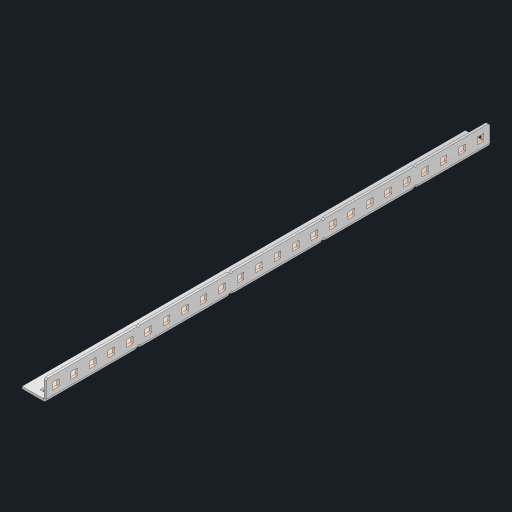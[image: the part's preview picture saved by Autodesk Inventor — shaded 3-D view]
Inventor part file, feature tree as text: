
AUTODESK INVENTOR PART (.ipt)
format: ipt  version: 2023 (Build 270158000, 158)  size: 847,360 bytes
history: native  units: in
note: dims shown in document units (in); Inventor stores cm internally (conversion verified against a paired STEP export)
features: other x53, extrude x47, sheet_metal_op x10, sketch x8, mirror x1, pattern_linear x1, chamfer x1
ambient origin geometry x8: Origin, YZ Plane, XZ Plane, XY Plane, X Axis, Y Axis, Z Axis, Center Point
bodies: Solid1 (feature_tree), Body (feature_tree)
feature tree (121):
  other  "Flange Pattern Plane"
  sheet_metal_op  "Flange Pattern"
  sheet_metal_op  "Body Pattern"
  other  "Arc Length"
  mirror  "Notch Mirror"
  pattern_linear  "Notch Pattern"  Spacing1=0.25in  [1 undecoded]
  chamfer  "End Chamfer"
  extrude  "Half Cut"  Depth=0.0625in
  sketch  "Sketch1"  dims[d0=1.5in]
  other  "Plate1"
  sketch  "Sketch2"  dims[d1=12.0in]
  other  "Plate2"
  sheet_metal_op  "Bend1"
  sheet_metal_op  "Corner1"
  sketch  "Sketch3"  dims[d2=0.0625in]
  other  "Flange Pattern Sketch"
  sketch  "Sketch7"  dims[d3=0.0625in]
  other  "Srf1"
  other  "Srf2"
  sketch  "Sketch8"  dims[d4=0.0312in]
  sketch  "Sketch9"  dims[d5=0.125in]
  other  "Srf91"
  sheet_metal_op  "Body Pattern Sketch"
  other  "Srf92"
  sketch  "Sketch13"  dims[d6=0.0625in]
  sketch  "Sketch14"  dims[d7=0.5in d8=90.0deg d9=0.0312in d10=0.25in d11=0.0625in d12=0.0625in d16=0.182in d17=0.02in d18=0.0625in d19=0.0in d20=0.25in d21=0.25in d46=0.172in d47=1.0in d48=0.0in d49=0.182in d50=0.02in d51=0.25in d52=0.25in d53=0.0625in d54=0.0in d55=0.172in d56=1.0in d57=0.0in d60=9.4488in d62=0.5in d63=0.3937in d65=0.5in d85=0.1473in d86=0.1782in d88=0.04in d89=0.0625in d90=0.0in d91=0.04in d92=0.0491in d95=2.5in d96=0.04in d97=0.25in d98=45.0deg d101=0.0in d102=2.497in d131=0.5in d132=9.4488in d134=0.5in d139=0.5in]
  other  "Srf856"
  other  "Srf1310"
  other  "Srf1311"
  other  "Srf1312"
  other  "Srf1376"
  other  "Srf1377"
  other  "Srf1728"
  other  "Srf1755"
  other  "Srf1878"
  other  "Srf1879"
  other  "Srf1880"
  other  "Srf1881"
  other  "Srf1882"
  other  "Srf1883"
  other  "Srf1884"
  other  "Srf1885"
  other  "Srf1886"
  other  "Srf1887"
  other  "Srf1888"
  other  "Srf1889"
  other  "Srf1890"
  other  "Srf1891"
  other  "Srf1892"
  other  "Srf1893"
  other  "Srf1894"
  other  "Srf1895"
  other  "Srf1942"
  other  "Srf1943"
  other  "Srf1944"
  other  "Srf1945"
  other  "Srf1946"
  other  "Srf1947"
  other  "Srf1948"
  other  "Srf1949"
  other  "Srf1950"
  other  "Srf1951"
  other  "Srf1952"
  other  "Srf1953"
  other  "Srf1954"
  other  "Srf1955"
  other  "Srf1956"
  other  "Srf1957"
  other  "Srf1958"
  other  "Srf1959"
  sheet_metal_op  "Flange Stamp"
  sheet_metal_op  "Flange Circle"
  sheet_metal_op  "Body Stamp"
  sheet_metal_op  "Body Circle"
  sheet_metal_op  "Notch"
  extrude  "ExtrusionSrf2"  Depth=0.0625in
  extrude  "ExtrusionSrf92"  Depth=0.5in
  extrude  "ExtrusionSrf856"  Depth=0.02in
  extrude  "ExtrusionSrf1310"  Depth=0.0625in
  extrude  "ExtrusionSrf1311"  TaperAngle=0.0deg  [1 undecoded]
  extrude  "ExtrusionSrf1312"  Depth=0.5in
  extrude  "ExtrusionSrf1376"  Depth=0.5in
  extrude  "ExtrusionSrf1377"  Depth=0.5in
  extrude  "ExtrusionSrf1728"  Depth=0.5in TaperAngle=0.0deg
  extrude  "ExtrusionSrf1755"  Depth=0.5in
  extrude  "ExtrusionSrf1878"  Depth=0.02in
  extrude  "ExtrusionSrf1879"  Depth=0.5in
  extrude  "ExtrusionSrf1880"  Depth=0.5in
  extrude  "ExtrusionSrf1881"  Depth=0.0625in
  extrude  "ExtrusionSrf1882"  TaperAngle=0.0deg  [1 undecoded]
  extrude  "ExtrusionSrf1883"  Depth=0.5in
  extrude  "ExtrusionSrf1884"  Depth=0.5in TaperAngle=0.0deg
  extrude  "ExtrusionSrf1885"  Depth=0.5in
  extrude  "ExtrusionSrf1886"  Depth=0.5in
  extrude  "ExtrusionSrf1887"  Depth=0.5in
  extrude  "ExtrusionSrf1888"  Depth=0.5in
  extrude  "ExtrusionSrf1889"  Depth=0.5in
  extrude  "ExtrusionSrf1890"  Depth=0.0625in
  extrude  "ExtrusionSrf1891"  TaperAngle=0.0deg  [1 undecoded]
  extrude  "ExtrusionSrf1892"  Depth=0.5in
  extrude  "ExtrusionSrf1893"  Depth=0.5in
  extrude  "ExtrusionSrf1894"  Depth=0.5in
  extrude  "ExtrusionSrf1895"  Depth=0.5in TaperAngle=45.0deg
  extrude  "ExtrusionSrf1942"  TaperAngle=0.0deg  [1 undecoded]
  extrude  "ExtrusionSrf1943"  Depth=0.5in
  extrude  "ExtrusionSrf1944"  Depth=0.5in
  extrude  "ExtrusionSrf1945"  Depth=0.5in
  extrude  "ExtrusionSrf1946"  Depth=0.5in
  extrude  "ExtrusionSrf1947"  Depth=0.5in
  extrude  "ExtrusionSrf1948"  [1 undecoded]
  extrude  "ExtrusionSrf1949"  [1 undecoded]
  extrude  "ExtrusionSrf1950"  [1 undecoded]
  extrude  "ExtrusionSrf1951"  [1 undecoded]
  extrude  "ExtrusionSrf1952"  [1 undecoded]
  extrude  "ExtrusionSrf1953"  [1 undecoded]
  extrude  "ExtrusionSrf1954"  [1 undecoded]
  extrude  "ExtrusionSrf1955"  [1 undecoded]
  extrude  "ExtrusionSrf1956"  [1 undecoded]
  extrude  "ExtrusionSrf1957"  [1 undecoded]
  extrude  "ExtrusionSrf1958"  [1 undecoded]
  extrude  "ExtrusionSrf1959"  [1 undecoded]
note: 17 required parameter values undecoded (feature->parameter linkage not recoverable at this tier; creation-order binding heuristic only, values carry confidence <= 0.55)
